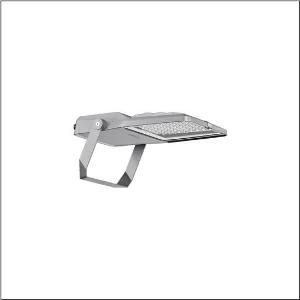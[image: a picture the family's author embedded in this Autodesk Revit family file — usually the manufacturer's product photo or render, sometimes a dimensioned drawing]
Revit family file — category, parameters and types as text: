
# Revit family: floodlight_fl_21_iq_mini___pl33t_5xa7771d2f1a_9c88
name_source: partatom
category: Lighting Fixtures
units: mm (PartAtom-declared; Revit-internal decimal feet)

## family parameters
Cut with Voids When Loaded = No
Host = Face
Light Source = No
Part Type = Normal
Room Calculation Point = No
Round Connector Dimension = Use Diameter
Shared = No

## types (1)
- --- (1 x LED, 17620 lm, 143 W, 3000K)
    Apparent Load = 143 VA
    CIE Flux Codes = 26 75 99 100 100
    Color Rendering = 70
    Color Temperature = 3000K
    Default Elevation = 1800 mm
    Description = Floodlight FL 21 iQ mini, floodlight, primary light control with lens, of PMMA, primary optical cover: protective disc, of toughened safety glass, transparent, light distribution: PL33T, light emission: direct distribution, installation type: surface-mounted, lamps: LED, High Power LED, rated values: 17.620lm | 143W | 123,2lm/W (begin service life); end service life: 17.620lm | 151,6W; at 50% lumin. flux: 8.810lm | 60,6W | 145,4lm/W, colour temperature: 3000K, colour rendering: CRI > 70, light colour: 730, light setting 1 begin service life: 100% | 17.620lm | 143W | 123,2lm/W | 3.000K, light setting 1 end service life: 151,6W, further light settings possible, control: Auto-Match, Temp-Guard, Lumen-Switch, Night-Set, Smart-Wire, Light-Fading, Desk-Remote (wireless, voltage-free reading and setting of iQ features in the workshop via application-optimized NFC function/RFID function), optimised constant luminous flux control (CLO 2.0), pre-setting: linear dimming characteristic, with terminal, 6-pole, mains connection: 220..240V, AC, 50/60Hz, luminaire housing, of diecast aluminium, powder-coated, SITECO metallic grey (DB 702S), corrosivity category C5 mid according to DIN EN ISO 12944suitable for swimming poolschlorine-resistant, sealing non-destructively replaceable, mounting bracket, of steel, galvanised, powder-coated, SITECO metallic grey (DB 702S), protection rating (complete): IP66, insulation class (complete): insulation class II (safety insulation), certification: CE, ENEC, VDE, protection symbol: D, impact resistance: IK08, permissible operating ambient temperature: -40..+40°C, permissible operating ambient temperature for outdoor applications: -40..+50°C, standard: DIN EN 12944, LABS conformity tested according to VDMA 24364:2018-05, packaging unit: 1 piece

Light Distribution: PL33T
    Height = 70 mm
    Lamp = 1 x LED
    Lamp Light Flux = 17620 lm
    Lamp Power = 143 W
    Lamp count = 1
    Length = 485 mm
    Luminous efficacy = 123 lm/W
    Manufacturer = Siteco
    ModVariant = No
    Model = 5XA7771D2F1A
    Mounting Place = Pole
    Mounting Type = Pole annexe
    Number of Poles = 1
    OnlyDefault = Yes
    Power Factor = 1
    Product Name = Floodlight FL 21 iQ mini | PL33T
    Product group = floodlight | pylon annexe
    ProductGroupID = 6201
    Protection Class = Protection class II
    Protection Degree = IP 66
    RLX_Detail_Level = 1
    RLX_Emergency_Light_Flux = 0 lm
    RLX_Emergency_Type = 0
    RLX_Emergency_Type_DB = No
    RlxData = <blob elided: 96765 chars, md5=2baab310>
    Socket = socket
    Standby Power = 0 W
    System Light Flux = 17620 lm
    System Power = 143 W
    Type Comments = factory setting: luminous flux: 100 % | dim-lin: 254 | 730 mA
    Type Image = l_1006845.jpg
    URL = http://relux.com
    VarID = @adj_150325
    Voltage = 0 V
    Weight = 0.00 kg
    Width = 337 mm

## geometry (parser evidence)
native form markers: Blend x4, Sweep x12
no freeform markers — native parametric forms only
